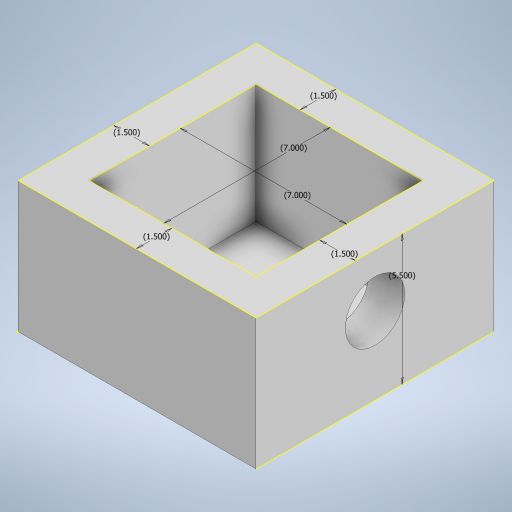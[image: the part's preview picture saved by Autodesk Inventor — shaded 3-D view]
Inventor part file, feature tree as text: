
AUTODESK INVENTOR PART (.ipt)
format: ipt  version: 2023 (Build 270158000, 158)  size: 244,224 bytes
history: native  units: in
note: dims shown in document units (in); Inventor stores cm internally (conversion verified against a paired STEP export)
features: sketch x8, extrude x4, shell x1
ambient origin geometry x8: Origin, YZ Plane, XZ Plane, XY Plane, X Axis, Y Axis, Z Axis, Center Point
bodies: Solid1 (feature_tree)
feature tree (13):
  extrude  "Extrusion1"  Depth=10.0in
  extrude  "Extrusion2"  Depth=0.5in
  shell  "Shell1"  Thickness=1.0in
  sketch  "Sketch3"  dims[d10=1.0in d11=1.0in]
  extrude  "Extrusion3"  Depth=1.0in
  sketch  "Sketch5"  dims[d15=5.0in d16=0.0in]
  sketch  "Sketch6"  dims[d17=1.5in]
  sketch  "Sketch7"  dims[d18=7.0in]
  extrude  "Extrusion4"  Depth=0.5in
  sketch  "Sketch1"  dims[d0=10.0in d1=10.0in]
  sketch  "Sketch2"  dims[d6=0.5in d7=0.0in d8=1.0in d9=1.0in]
  sketch  "Sketch4"  dims[d12=5.0in d13=0.0in d14=0.5in]
  sketch  "Sketch8"  dims[d19=7.0in d20=1.5in d21=1.5in d22=1.5in d23=5.5in d24=2.25in d25=5.0in d26=2.5in d27=2.0in d28=0.0in d29=0.5in d30=0.0344in]
